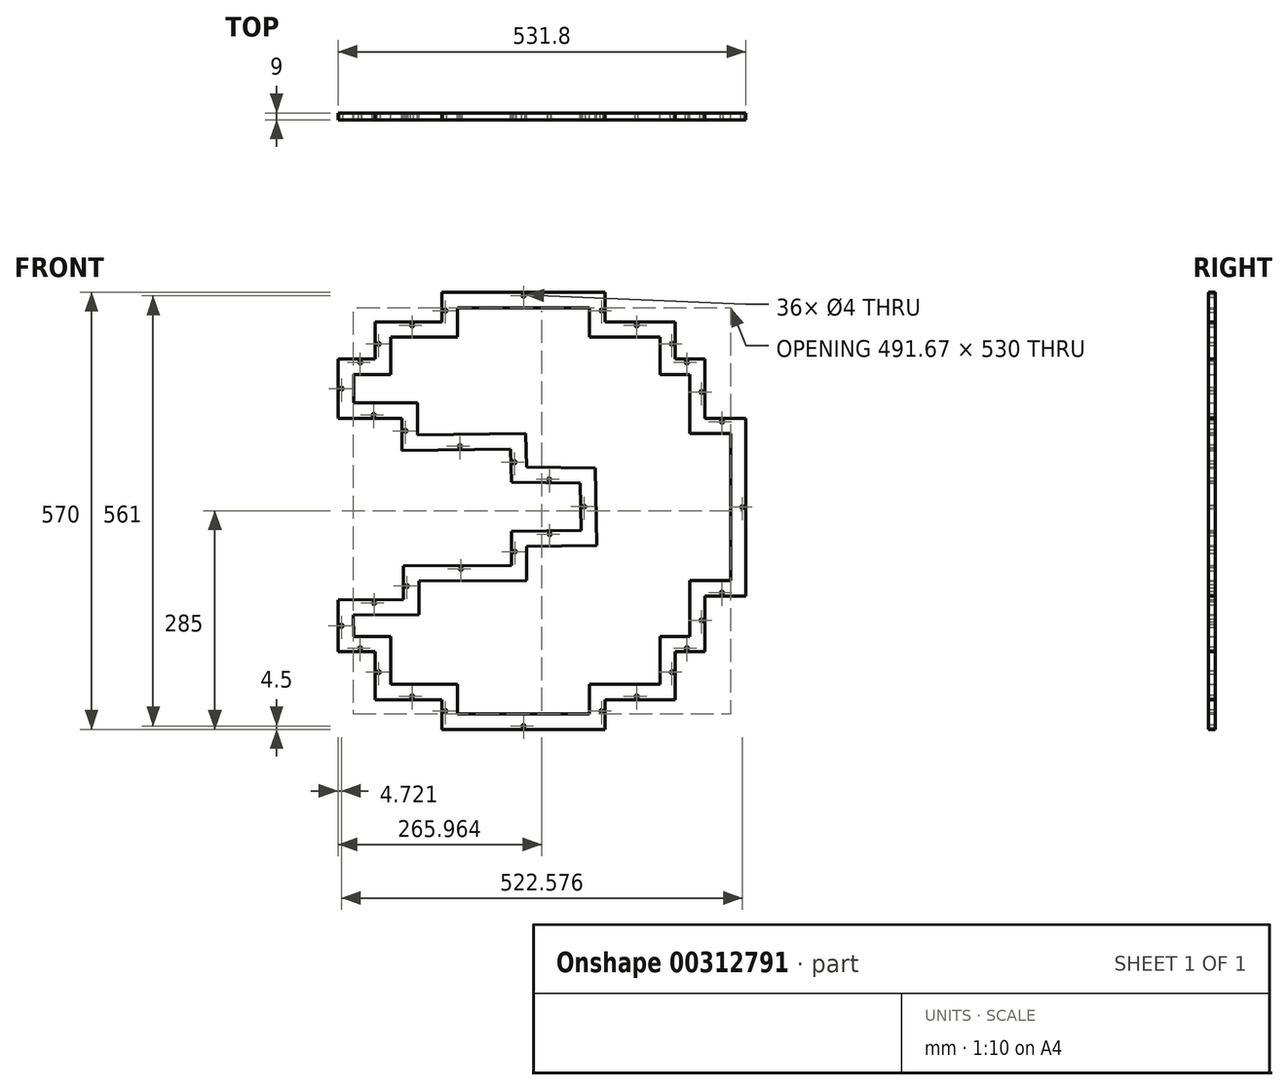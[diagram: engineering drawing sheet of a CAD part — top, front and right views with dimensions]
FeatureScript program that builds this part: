
annotation { "Feature Type Name" : "Feature", "Feature Type Description" : "" }
export const myFeature = defineFeature(function(context is Context, id is Id, definition is map)
    precondition{}
    {
        {
            var Q0;
            Q0=qCreatedBy(makeId("Front.planeOp"),FACE);
            var sketch = newSketch(context, id + "F0", { "sketchPlane" : qUnion([Q0])});
            skLineSegment(sketch, "E0", {"start": v(265.9, 120.76) * mm, "end": v(212.76, 120.76) * mm});
            skLineSegment(sketch, "E1", {"start": v(212.76, 120.76) * mm, "end": v(212.76, 198.05) * mm});
            skLineSegment(sketch, "E2", {"start": v(212.76, 198.05) * mm, "end": v(174.11, 198.05) * mm});
            skLineSegment(sketch, "E3", {"start": v(174.11, 198.05) * mm, "end": v(174.11, 246.35) * mm});
            skLineSegment(sketch, "E4", {"start": v(174.11, 246.35) * mm, "end": v(82.34, 246.35) * mm});
            skLineSegment(sketch, "E5", {"start": v(82.34, 246.35) * mm, "end": v(82.34, 285) * mm});
            skLineSegment(sketch, "E6", {"start": v(82.34, 285) * mm, "end": v(-130.2, 285) * mm});
            skLineSegment(sketch, "E7", {"start": v(-130.2, 285) * mm, "end": v(-130.2, 246.35) * mm});
            skLineSegment(sketch, "E8", {"start": v(-130.2, 246.35) * mm, "end": v(-217.15, 246.35) * mm});
            skLineSegment(sketch, "E9", {"start": v(-217.15, 246.35) * mm, "end": v(-217.15, 198.05) * mm});
            skLineSegment(sketch, "E10", {"start": v(-217.15, 198.05) * mm, "end": v(-265.46, 198.05) * mm});
            skLineSegment(sketch, "E11", {"start": v(-265.46, 198.05) * mm, "end": v(-265.46, 120.76) * mm});
            skLineSegment(sketch, "E12", {"start": v(-265.46, 120.76) * mm, "end": v(-182.22, 120.66) * mm});
            skLineSegment(sketch, "E13", {"start": v(-182.22, 120.66) * mm, "end": v(-182.3, 79) * mm});
            skLineSegment(sketch, "E14", {"start": v(-182.3, 79) * mm, "end": v(-40.62, 80.76) * mm});
            skLineSegment(sketch, "E15", {"start": v(-40.62, 80.76) * mm, "end": v(-39.72, 37.15) * mm});
            skLineSegment(sketch, "E16", {"start": v(-39.72, 37.15) * mm, "end": v(50.2, 36.25) * mm});
            skLineSegment(sketch, "E17", {"start": v(50.2, 36.25) * mm, "end": v(51.12, -25.52) * mm});
            skLineSegment(sketch, "E18", {"start": v(51.12, -25.52) * mm, "end": v(-39.72, -26.43) * mm});
            skLineSegment(sketch, "E19", {"start": v(-39.72, -26.43) * mm, "end": v(-39.72, -70.94) * mm});
            skLineSegment(sketch, "E20", {"start": v(-39.72, -70.94) * mm, "end": v(-180.51, -71.85) * mm});
            skLineSegment(sketch, "E21", {"start": v(-180.51, -71.85) * mm, "end": v(-180.51, -115.45) * mm});
            skLineSegment(sketch, "E22", {"start": v(-180.51, -115.45) * mm, "end": v(-265.9, -116.36) * mm});
            skLineSegment(sketch, "E23", {"start": v(-265.9, -116.36) * mm, "end": v(-265.46, -183.56) * mm});
            skLineSegment(sketch, "E24", {"start": v(-265.46, -183.56) * mm, "end": v(-217.15, -183.56) * mm});
            skLineSegment(sketch, "E25", {"start": v(-217.15, -183.56) * mm, "end": v(-217.15, -246.36) * mm});
            skLineSegment(sketch, "E26", {"start": v(-217.15, -246.36) * mm, "end": v(-130.2, -246.36) * mm});
            skLineSegment(sketch, "E27", {"start": v(-130.2, -246.36) * mm, "end": v(-130.2, -285) * mm});
            skLineSegment(sketch, "E28", {"start": v(-130.2, -285) * mm, "end": v(82.34, -285) * mm});
            skLineSegment(sketch, "E29", {"start": v(82.34, -285) * mm, "end": v(82.34, -246.36) * mm});
            skLineSegment(sketch, "E30", {"start": v(82.34, -246.36) * mm, "end": v(174.11, -246.36) * mm});
            skLineSegment(sketch, "E31", {"start": v(174.11, -246.36) * mm, "end": v(174.11, -183.56) * mm});
            skLineSegment(sketch, "E32", {"start": v(174.11, -183.56) * mm, "end": v(212.76, -183.56) * mm});
            skLineSegment(sketch, "E33", {"start": v(212.76, -183.56) * mm, "end": v(212.76, -111.1) * mm});
            skLineSegment(sketch, "E34", {"start": v(212.76, -111.1) * mm, "end": v(265.9, -111.1) * mm});
            skLineSegment(sketch, "E35", {"start": v(265.9, -111.1) * mm, "end": v(265.9, 120.76) * mm});
            skLineSegment(sketch, "E36.0", {"start": v(261.4, 116.26) * mm, "end": v(208.26, 116.26) * mm, "construction": true});
            skLineSegment(sketch, "E36.1", {"start": v(261.4, -106.6) * mm, "end": v(261.4, 116.26) * mm, "construction": true});
            skLineSegment(sketch, "E36.2", {"start": v(208.26, -106.6) * mm, "end": v(261.4, -106.6) * mm, "construction": true});
            skLineSegment(sketch, "E36.3", {"start": v(208.26, -179.06) * mm, "end": v(208.26, -106.6) * mm, "construction": true});
            skLineSegment(sketch, "E36.4", {"start": v(169.61, -179.06) * mm, "end": v(208.26, -179.06) * mm, "construction": true});
            skLineSegment(sketch, "E36.5", {"start": v(169.61, -241.86) * mm, "end": v(169.61, -179.06) * mm, "construction": true});
            skLineSegment(sketch, "E36.6", {"start": v(77.84, -241.86) * mm, "end": v(169.61, -241.86) * mm, "construction": true});
            skLineSegment(sketch, "E36.7", {"start": v(77.84, -280.5) * mm, "end": v(77.84, -241.86) * mm, "construction": true});
            skLineSegment(sketch, "E36.8", {"start": v(-125.7, -280.5) * mm, "end": v(77.84, -280.5) * mm, "construction": true});
            skLineSegment(sketch, "E36.9", {"start": v(-125.7, -241.86) * mm, "end": v(-125.7, -280.5) * mm, "construction": true});
            skLineSegment(sketch, "E36.10", {"start": v(-212.65, -241.86) * mm, "end": v(-125.7, -241.86) * mm, "construction": true});
            skLineSegment(sketch, "E36.11", {"start": v(208.26, 116.26) * mm, "end": v(208.26, 193.55) * mm, "construction": true});
            skLineSegment(sketch, "E36.12", {"start": v(-212.65, -179.06) * mm, "end": v(-212.65, -241.86) * mm, "construction": true});
            skLineSegment(sketch, "E36.13", {"start": v(-261, -179.06) * mm, "end": v(-212.65, -179.06) * mm, "construction": true});
            skLineSegment(sketch, "E36.14", {"start": v(-260.96, 193.55) * mm, "end": v(-260.96, 125.26) * mm, "construction": true});
            skLineSegment(sketch, "E36.15", {"start": v(-212.65, 193.55) * mm, "end": v(-260.96, 193.55) * mm, "construction": true});
            skLineSegment(sketch, "E36.16", {"start": v(-212.65, 241.85) * mm, "end": v(-212.65, 193.55) * mm, "construction": true});
            skLineSegment(sketch, "E36.17", {"start": v(-125.7, 241.85) * mm, "end": v(-212.65, 241.85) * mm, "construction": true});
            skLineSegment(sketch, "E36.18", {"start": v(-125.7, 280.5) * mm, "end": v(-125.7, 241.85) * mm, "construction": true});
            skLineSegment(sketch, "E36.19", {"start": v(77.84, 280.5) * mm, "end": v(-125.7, 280.5) * mm, "construction": true});
            skLineSegment(sketch, "E36.20", {"start": v(208.26, 193.55) * mm, "end": v(169.61, 193.55) * mm, "construction": true});
            skLineSegment(sketch, "E36.21", {"start": v(169.61, 193.55) * mm, "end": v(169.61, 241.85) * mm, "construction": true});
            skLineSegment(sketch, "E36.22", {"start": v(169.61, 241.85) * mm, "end": v(77.84, 241.85) * mm, "construction": true});
            skLineSegment(sketch, "E36.23", {"start": v(77.84, 241.85) * mm, "end": v(77.84, 280.5) * mm, "construction": true});
            skLineSegment(sketch, "E36.24", {"start": v(-260.96, 125.26) * mm, "end": v(-177.7, 125.15) * mm, "construction": true});
            skLineSegment(sketch, "E36.25", {"start": v(-177.7, 125.15) * mm, "end": v(-177.78, 83.55) * mm, "construction": true});
            skLineSegment(sketch, "E36.26", {"start": v(-177.78, 83.55) * mm, "end": v(-36.22, 85.31) * mm, "construction": true});
            skLineSegment(sketch, "E36.27", {"start": v(-36.22, 85.31) * mm, "end": v(-35.3, 41.6) * mm, "construction": true});
            skLineSegment(sketch, "E36.28", {"start": v(-35.3, 41.6) * mm, "end": v(54.64, 40.7) * mm, "construction": true});
            skLineSegment(sketch, "E36.29", {"start": v(54.64, 40.7) * mm, "end": v(55.69, -29.97) * mm, "construction": true});
            skLineSegment(sketch, "E36.30", {"start": v(55.69, -29.97) * mm, "end": v(-35.22, -30.88) * mm, "construction": true});
            skLineSegment(sketch, "E36.31", {"start": v(-35.22, -30.88) * mm, "end": v(-35.22, -75.4) * mm, "construction": true});
            skLineSegment(sketch, "E36.32", {"start": v(-35.22, -75.4) * mm, "end": v(-176.01, -76.32) * mm, "construction": true});
            skLineSegment(sketch, "E36.33", {"start": v(-176.01, -76.32) * mm, "end": v(-176.01, -119.9) * mm, "construction": true});
            skLineSegment(sketch, "E36.34", {"start": v(-176.01, -119.9) * mm, "end": v(-261.37, -120.82) * mm, "construction": true});
            skLineSegment(sketch, "E36.35", {"start": v(-261.37, -120.82) * mm, "end": v(-261, -179.06) * mm, "construction": true});
            skCircle(sketch, "E37", {"center": v(-23.93, 280.5) * mm, "radius": 2 * mm});
            skCircle(sketch, "E38", {"center": v(-125.7, 261.18) * mm, "radius": 2 * mm});
            skCircle(sketch, "E39", {"center": v(-169.17, 241.85) * mm, "radius": 2 * mm});
            skCircle(sketch, "E40", {"center": v(-212.65, 217.7) * mm, "radius": 2 * mm});
            skCircle(sketch, "E41", {"center": v(-236.8, 193.55) * mm, "radius": 2 * mm});
            skCircle(sketch, "E42", {"center": v(-260.96, 159.4) * mm, "radius": 2 * mm});
            skCircle(sketch, "E43", {"center": v(-219.33, 125.2) * mm, "radius": 2 * mm});
            skCircle(sketch, "E44", {"center": v(-177.75, 104.35) * mm, "radius": 2 * mm});
            skCircle(sketch, "E45", {"center": v(-107, 84.43) * mm, "radius": 2 * mm});
            skCircle(sketch, "E46", {"center": v(-35.76, 63.46) * mm, "radius": 2 * mm});
            skCircle(sketch, "E47", {"center": v(9.67, 41.16) * mm, "radius": 2 * mm});
            skCircle(sketch, "E48", {"center": v(77.84, 261.18) * mm, "radius": 2 * mm});
            skCircle(sketch, "E49", {"center": v(123.73, 241.85) * mm, "radius": 2 * mm});
            skCircle(sketch, "E50", {"center": v(169.61, 217.7) * mm, "radius": 2 * mm});
            skCircle(sketch, "E51", {"center": v(188.94, 193.55) * mm, "radius": 2 * mm});
            skCircle(sketch, "E52", {"center": v(208.26, 154.9) * mm, "radius": 2 * mm});
            skCircle(sketch, "E53", {"center": v(234.83, 116.26) * mm, "radius": 2 * mm});
            skCircle(sketch, "E54", {"center": v(261.4, 4.83) * mm, "radius": 2 * mm});
            skCircle(sketch, "E55", {"center": v(234.83, -106.6) * mm, "radius": 2 * mm});
            skCircle(sketch, "E56", {"center": v(55.17, 5.36) * mm, "radius": 2 * mm});
            skCircle(sketch, "E57", {"center": v(10.24, -30.43) * mm, "radius": 2 * mm});
            skCircle(sketch, "E58", {"center": v(-35.22, -53.15) * mm, "radius": 2 * mm});
            skCircle(sketch, "E59", {"center": v(-105.61, -75.86) * mm, "radius": 2 * mm});
            skCircle(sketch, "E60", {"center": v(-176.01, -98.1) * mm, "radius": 2 * mm});
            skCircle(sketch, "E61", {"center": v(-218.69, -120.36) * mm, "radius": 2 * mm});
            skCircle(sketch, "E62", {"center": v(-261.18, -149.94) * mm, "radius": 2 * mm});
            skCircle(sketch, "E63", {"center": v(-236.82, -179.06) * mm, "radius": 2 * mm});
            skCircle(sketch, "E64", {"center": v(-212.65, -210.46) * mm, "radius": 2 * mm});
            skCircle(sketch, "E65", {"center": v(-169.17, -241.86) * mm, "radius": 2 * mm});
            skCircle(sketch, "E66", {"center": v(-125.7, -261.18) * mm, "radius": 2 * mm});
            skCircle(sketch, "E67", {"center": v(-23.93, -280.5) * mm, "radius": 2 * mm});
            skCircle(sketch, "E68", {"center": v(77.84, -261.18) * mm, "radius": 2 * mm});
            skCircle(sketch, "E69", {"center": v(123.73, -241.86) * mm, "radius": 2 * mm});
            skCircle(sketch, "E70", {"center": v(169.61, -210.46) * mm, "radius": 2 * mm});
            skCircle(sketch, "E71", {"center": v(188.94, -179.06) * mm, "radius": 2 * mm});
            skCircle(sketch, "E72", {"center": v(208.26, -142.83) * mm, "radius": 2 * mm});
            skSolve(sketch);
        }
        {
            var Q0;
            Q0=qSketchRegion(id+"F0",true);
            extrude(context, id + "F1", {"entities" : qUnion([Q0]), "depth" : 9 * mm});
        }
        {
            var Q0;
            Q0=makeQuery(id+"F1.opExtrude","CAP_FACE",FACE,{"disambiguationData":[OSD([sQuery(id+"F0.wireOp",EDGE,"E0"),sQuery(id+"F0.wireOp",EDGE,"E1"),sQuery(id+"F0.wireOp",EDGE,"E2"),sQuery(id+"F0.wireOp",EDGE,"E3"),sQuery(id+"F0.wireOp",EDGE,"E4"),sQuery(id+"F0.wireOp",EDGE,"E5"),sQuery(id+"F0.wireOp",EDGE,"E6"),sQuery(id+"F0.wireOp",EDGE,"E7"),sQuery(id+"F0.wireOp",EDGE,"E8"),sQuery(id+"F0.wireOp",EDGE,"E9"),sQuery(id+"F0.wireOp",EDGE,"E10"),sQuery(id+"F0.wireOp",EDGE,"E11"),sQuery(id+"F0.wireOp",EDGE,"E12"),sQuery(id+"F0.wireOp",EDGE,"E13"),sQuery(id+"F0.wireOp",EDGE,"E14"),sQuery(id+"F0.wireOp",EDGE,"E15"),sQuery(id+"F0.wireOp",EDGE,"E16"),sQuery(id+"F0.wireOp",EDGE,"E17"),sQuery(id+"F0.wireOp",EDGE,"E18"),sQuery(id+"F0.wireOp",EDGE,"E19"),sQuery(id+"F0.wireOp",EDGE,"E20"),sQuery(id+"F0.wireOp",EDGE,"E21"),sQuery(id+"F0.wireOp",EDGE,"E22"),sQuery(id+"F0.wireOp",EDGE,"E23"),sQuery(id+"F0.wireOp",EDGE,"E24"),sQuery(id+"F0.wireOp",EDGE,"E25"),sQuery(id+"F0.wireOp",EDGE,"E26"),sQuery(id+"F0.wireOp",EDGE,"E27"),sQuery(id+"F0.wireOp",EDGE,"E28"),sQuery(id+"F0.wireOp",EDGE,"E29"),sQuery(id+"F0.wireOp",EDGE,"E30"),sQuery(id+"F0.wireOp",EDGE,"E31"),sQuery(id+"F0.wireOp",EDGE,"E32"),sQuery(id+"F0.wireOp",EDGE,"E33"),sQuery(id+"F0.wireOp",EDGE,"E34"),sQuery(id+"F0.wireOp",EDGE,"E35"),sQuery(id+"F0.wireOp",EDGE,"E37"),sQuery(id+"F0.wireOp",EDGE,"E38"),sQuery(id+"F0.wireOp",EDGE,"E39"),sQuery(id+"F0.wireOp",EDGE,"E40"),sQuery(id+"F0.wireOp",EDGE,"E41"),sQuery(id+"F0.wireOp",EDGE,"E42"),sQuery(id+"F0.wireOp",EDGE,"E43"),sQuery(id+"F0.wireOp",EDGE,"E44"),sQuery(id+"F0.wireOp",EDGE,"E45"),sQuery(id+"F0.wireOp",EDGE,"E46"),sQuery(id+"F0.wireOp",EDGE,"E47"),sQuery(id+"F0.wireOp",EDGE,"E48"),sQuery(id+"F0.wireOp",EDGE,"E49"),sQuery(id+"F0.wireOp",EDGE,"E50"),sQuery(id+"F0.wireOp",EDGE,"E51"),sQuery(id+"F0.wireOp",EDGE,"E52"),sQuery(id+"F0.wireOp",EDGE,"E53"),sQuery(id+"F0.wireOp",EDGE,"E54"),sQuery(id+"F0.wireOp",EDGE,"E55"),sQuery(id+"F0.wireOp",EDGE,"E56"),sQuery(id+"F0.wireOp",EDGE,"E57"),sQuery(id+"F0.wireOp",EDGE,"E58"),sQuery(id+"F0.wireOp",EDGE,"E59"),sQuery(id+"F0.wireOp",EDGE,"E60"),sQuery(id+"F0.wireOp",EDGE,"E61"),sQuery(id+"F0.wireOp",EDGE,"E62"),sQuery(id+"F0.wireOp",EDGE,"E63"),sQuery(id+"F0.wireOp",EDGE,"E64"),sQuery(id+"F0.wireOp",EDGE,"E65"),sQuery(id+"F0.wireOp",EDGE,"E66"),sQuery(id+"F0.wireOp",EDGE,"E67"),sQuery(id+"F0.wireOp",EDGE,"E68"),sQuery(id+"F0.wireOp",EDGE,"E69"),sQuery(id+"F0.wireOp",EDGE,"E70"),sQuery(id+"F0.wireOp",EDGE,"E71"),sQuery(id+"F0.wireOp",EDGE,"E72")])],"isStart":true});
            var sketch = newSketch(context, id + "F2", { "sketchPlane" : qUnion([Q0])});
            skLineSegment(sketch, "E73.0", {"start": v(-62.34, 226.35) * mm, "end": v(-62.34, 265) * mm});
            skLineSegment(sketch, "E73.1", {"start": v(-154.11, 226.35) * mm, "end": v(-62.34, 226.35) * mm});
            skLineSegment(sketch, "E73.2", {"start": v(-154.11, 178.05) * mm, "end": v(-154.11, 226.35) * mm});
            skLineSegment(sketch, "E73.3", {"start": v(-192.76, 178.05) * mm, "end": v(-154.11, 178.05) * mm});
            skLineSegment(sketch, "E73.4", {"start": v(-192.76, 100.76) * mm, "end": v(-192.76, 178.05) * mm});
            skLineSegment(sketch, "E73.5", {"start": v(-245.9, 100.76) * mm, "end": v(-192.76, 100.76) * mm});
            skLineSegment(sketch, "E73.6", {"start": v(-245.9, -91.1) * mm, "end": v(-245.9, 100.76) * mm});
            skLineSegment(sketch, "E73.7", {"start": v(-192.76, -91.1) * mm, "end": v(-245.9, -91.1) * mm});
            skLineSegment(sketch, "E73.8", {"start": v(-192.76, -163.56) * mm, "end": v(-192.76, -91.1) * mm});
            skLineSegment(sketch, "E73.9", {"start": v(-154.11, -163.56) * mm, "end": v(-192.76, -163.56) * mm});
            skLineSegment(sketch, "E73.10", {"start": v(-154.11, -226.36) * mm, "end": v(-154.11, -163.56) * mm});
            skLineSegment(sketch, "E73.11", {"start": v(-62.34, 265) * mm, "end": v(110.2, 265) * mm});
            skLineSegment(sketch, "E73.12", {"start": v(-62.34, -226.36) * mm, "end": v(-154.11, -226.36) * mm});
            skLineSegment(sketch, "E73.13", {"start": v(-62.34, -265) * mm, "end": v(-62.34, -226.36) * mm});
            skLineSegment(sketch, "E73.14", {"start": v(20.12, 56.96) * mm, "end": v(-69.92, 56.05) * mm});
            skLineSegment(sketch, "E73.15", {"start": v(21.04, 101) * mm, "end": v(20.12, 56.96) * mm});
            skLineSegment(sketch, "E73.16", {"start": v(162.25, 99.25) * mm, "end": v(21.04, 101) * mm});
            skLineSegment(sketch, "E73.17", {"start": v(162.18, 140.63) * mm, "end": v(162.25, 99.25) * mm});
            skLineSegment(sketch, "E73.18", {"start": v(245.46, 140.74) * mm, "end": v(162.18, 140.63) * mm});
            skLineSegment(sketch, "E73.19", {"start": v(245.46, 178.05) * mm, "end": v(245.46, 140.74) * mm});
            skLineSegment(sketch, "E73.20", {"start": v(110.2, 265) * mm, "end": v(110.2, 226.35) * mm});
            skLineSegment(sketch, "E73.21", {"start": v(110.2, 226.35) * mm, "end": v(197.15, 226.35) * mm});
            skLineSegment(sketch, "E73.22", {"start": v(197.15, 226.35) * mm, "end": v(197.15, 178.05) * mm});
            skLineSegment(sketch, "E73.23", {"start": v(197.15, 178.05) * mm, "end": v(245.46, 178.05) * mm});
            skLineSegment(sketch, "E73.24", {"start": v(-69.92, 56.05) * mm, "end": v(-71.42, -45.32) * mm});
            skLineSegment(sketch, "E73.25", {"start": v(-71.42, -45.32) * mm, "end": v(19.72, -46.23) * mm});
            skLineSegment(sketch, "E73.26", {"start": v(19.72, -46.23) * mm, "end": v(19.72, -90.8) * mm});
            skLineSegment(sketch, "E73.27", {"start": v(19.72, -90.8) * mm, "end": v(160.51, -91.72) * mm});
            skLineSegment(sketch, "E73.28", {"start": v(160.51, -91.72) * mm, "end": v(160.51, -135.23) * mm});
            skLineSegment(sketch, "E73.29", {"start": v(160.51, -135.23) * mm, "end": v(245.77, -136.15) * mm});
            skLineSegment(sketch, "E73.30", {"start": v(245.77, -136.15) * mm, "end": v(245.6, -163.56) * mm});
            skLineSegment(sketch, "E73.31", {"start": v(245.6, -163.56) * mm, "end": v(197.15, -163.56) * mm});
            skLineSegment(sketch, "E73.32", {"start": v(197.15, -163.56) * mm, "end": v(197.15, -226.36) * mm});
            skLineSegment(sketch, "E73.33", {"start": v(197.15, -226.36) * mm, "end": v(110.2, -226.36) * mm});
            skLineSegment(sketch, "E73.34", {"start": v(110.2, -226.36) * mm, "end": v(110.2, -265) * mm});
            skLineSegment(sketch, "E73.35", {"start": v(110.2, -265) * mm, "end": v(-62.34, -265) * mm});
            skSolve(sketch);
        }
        {
            var Q0;
            Q0=makeQuery(id+"F2.imprint","IMPRINT",FACE,{"disambiguationData":[TD([[makeQuery(id+"F2.imprint","IMPRINT",EDGE,{"derivedFrom":sQuery(id+"F2.wireOp",EDGE,"E73.0")}),-1.0]])]});
            extrude(context, id + "F3", {"entities" : qUnion([Q0]), "operationType" : NewBodyOperationType.REMOVE, "endBound" : BoundingType.THROUGH_ALL, "oppositeDirection" : true, "depth" : 25 * mm});
        }
    });
